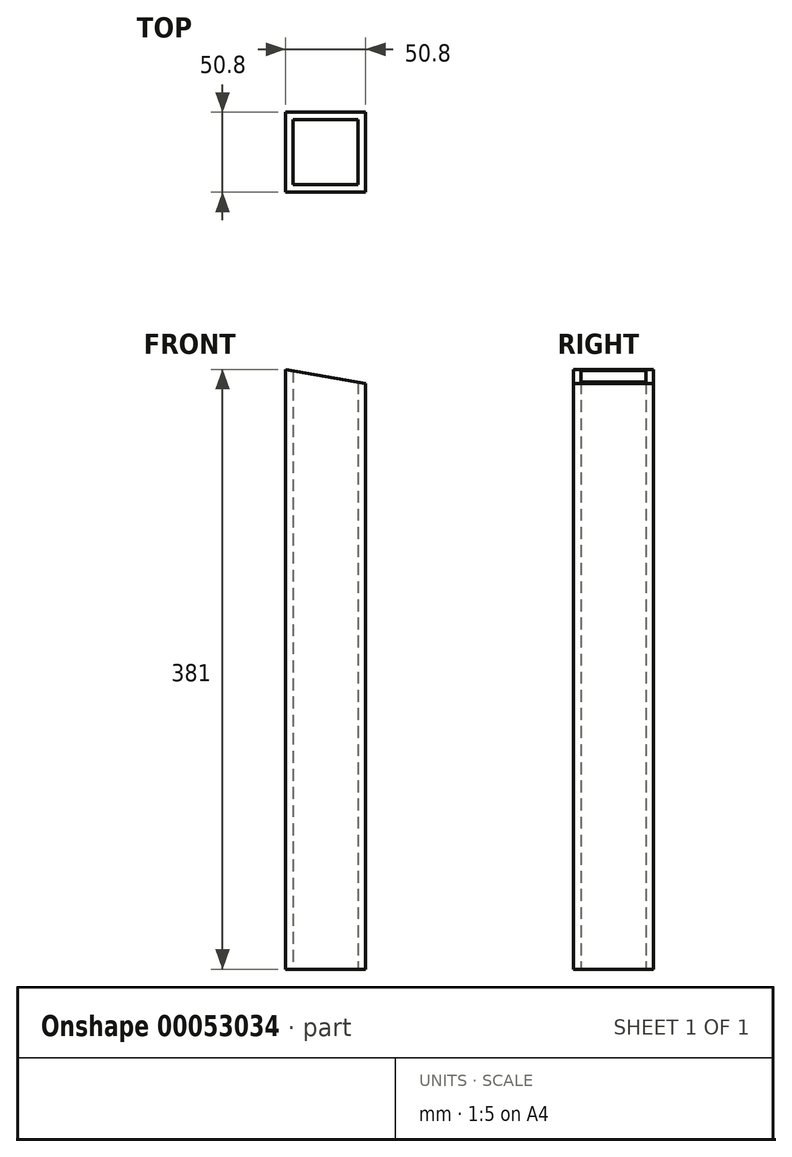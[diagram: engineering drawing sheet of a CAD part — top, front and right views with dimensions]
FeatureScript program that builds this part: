
annotation { "Feature Type Name" : "Feature", "Feature Type Description" : "" }
export const myFeature = defineFeature(function(context is Context, id is Id, definition is map)
    precondition{}
    {
        {
            var Q0;
            Q0=qCreatedBy(makeId("Top.planeOp"),FACE);
            var sketch = newSketch(context, id + "F0", { "sketchPlane" : qUnion([Q0])});
            skLineSegment(sketch, "E0.bottom", {"start": v(0, 0) * mm, "end": v(-50.8, 0) * mm});
            skLineSegment(sketch, "E0.top", {"start": v(0, 50.8) * mm, "end": v(-50.8, 50.8) * mm});
            skLineSegment(sketch, "E0.left", {"start": v(0, 0) * mm, "end": v(0, 50.8) * mm});
            skLineSegment(sketch, "E0.right", {"start": v(-50.8, 0) * mm, "end": v(-50.8, 50.8) * mm});
            skLineSegment(sketch, "E1.bottom", {"start": v(-46.04, 46.04) * mm, "end": v(-4.76, 46.04) * mm});
            skLineSegment(sketch, "E1.top", {"start": v(-46.04, 4.76) * mm, "end": v(-4.76, 4.76) * mm});
            skLineSegment(sketch, "E1.left", {"start": v(-46.04, 46.04) * mm, "end": v(-46.04, 4.76) * mm});
            skLineSegment(sketch, "E1.right", {"start": v(-4.76, 46.04) * mm, "end": v(-4.76, 4.76) * mm});
            skSolve(sketch);
        }
        {
            var Q0;
            Q0=makeQuery(id+"F0.imprint","IMPRINT",FACE,{"disambiguationData":[TD([[makeQuery(id+"F0.imprint","IMPRINT",EDGE,{"derivedFrom":sQuery(id+"F0.wireOp",EDGE,"E0.bottom")}),-1.0]])]});
            extrude(context, id + "F1", {"entities" : qUnion([Q0]), "depth" : 381 * mm});
        }
        {
            var Q0;
            Q0=makeQuery(id+"F1.opExtrude","SWEPT_FACE",FACE,{"disambiguationData":[OSD([sQuery(id+"F0.wireOp",EDGE,"E0.bottom")])]});
            var sketch = newSketch(context, id + "F2", { "sketchPlane" : qUnion([Q0])});
            skLineSegment(sketch, "E2", {"start": v(0, 381) * mm, "end": v(-50.8, 381) * mm});
            skLineSegment(sketch, "E3", {"start": v(-50.8, 381) * mm, "end": v(0, 372.04) * mm});
            skLineSegment(sketch, "E4", {"start": v(0, 372.04) * mm, "end": v(0, 381) * mm});
            skSolve(sketch);
        }
        {
            var Q0;
            Q0=makeQuery(id+"F2.imprint","IMPRINT",FACE,{"disambiguationData":[TD([[makeQuery(id+"F2.imprint","IMPRINT",EDGE,{"derivedFrom":sQuery(id+"F2.wireOp",EDGE,"E2")}),1.0]])]});
            extrude(context, id + "F3", {"entities" : qUnion([Q0]), "operationType" : NewBodyOperationType.REMOVE, "endBound" : BoundingType.THROUGH_ALL, "oppositeDirection" : true, "depth" : 25.4 * mm});
        }
    });
